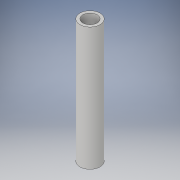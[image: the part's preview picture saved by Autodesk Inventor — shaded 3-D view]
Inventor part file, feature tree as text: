
AUTODESK INVENTOR PART (.ipt)
format: ipt  version: 2019.4 (Build 234330000, 330)  size: 94,720 bytes
history: native  units: mm
features: extrude x1, sketch x1
ambient origin geometry x8: Origin, YZ Plane, XZ Plane, XY Plane, X Axis, Y Axis, Z Axis, Center Point
bodies: Solid1 (feature_tree)
feature tree (2):
  extrude  "Extrusion1"  Depth=43.0mm
  sketch  "Sketch1"  dims[d0=5.0mm d1=7.0mm d2=43.0mm d3=0.0mm]
